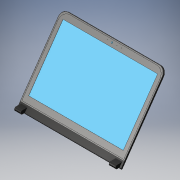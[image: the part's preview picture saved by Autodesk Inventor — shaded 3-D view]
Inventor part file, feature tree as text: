
AUTODESK INVENTOR PART (.ipt)
format: ipt  version: 2025 (Build 290162000, 162)  size: 221,184 bytes
history: native  units: in
note: dims shown in document units (in); Inventor stores cm internally (conversion verified against a paired STEP export)
features: sketch x10, extrude x7, hole x2, move_body x2, other x1, plane x1, pattern_linear x1
ambient origin geometry x8: Origin, YZ Plane, XZ Plane, XY Plane, X Axis, Y Axis, Z Axis, Center Point
bodies: Solid1 (feature_tree)
feature tree (24):
  other  "MONITOR"
  extrude  "SCREEN"  Depth=12.9921in
  extrude  "CAMERA"  Depth=0.1969in TaperAngle=0.0deg
  hole  "CAMERA "  [1 undecoded]
  hole  "AESTHETICS"  [1 undecoded]
  extrude  "SIDE BAND"  Depth=9.0354in
  extrude  "SIDE BAND 1"  Depth=12.9528in
  extrude  "CUT"  Depth=12.7165in
  extrude  "ROUND BASE"  Depth=0.9252in
  plane  "Work Plane1"
  extrude  "HINGE"  Depth=12.9921in TaperAngle=0.0deg
  pattern_linear  "HINGE 1"  Count1=33 Spacing1=0.0in
  move_body  "Move Body1"
  move_body  "Move Body2"
  sketch  "Sketch1"  dims[d2=12.9921in d3=9.8425in]
  sketch  "Sketch2"  dims[d4=0.7874in d5=0.1969in d6=0.0in]
  sketch  "Sketch3"  dims[d9=11.811in d10=7.4803in]
  sketch  "Sketch4"  dims[d11=0.0197in d12=0.0in d14=0.0098in d15=0.0in]
  sketch  "Sketch5"  dims[d16=0.0394in d17=0.2953in d18=0.1476in d19=0.0984in d20=90.0deg d21=0.0039in d22=0.8108in]
  sketch  "Sketch6"  dims[d23=0.0394in d24=0.2953in d25=0.1476in d26=0.0984in d27=90.0deg d28=0.0039in d29=0.8108in d36=9.0354in]
  sketch  "Sketch7"  dims[d37=0.8071in d38=12.9528in]
  sketch  "Sketch8"  dims[d39=0.0059in d40=0.0in d47=12.7165in]
  sketch  "Sketch9"  dims[d48=8.7992in d49=0.9252in]
  sketch  "Sketch10"  dims[d50=0.0059in d51=0.0in d52=12.9921in d53=0.0in d54=12.9921in d55=0.0in d56=5.9055in d58=0.315in d60=0.5512in d62=0.6311in d63=0.2258in d64=0.7874in d65=0.0in d66=0.7874in d68=11.811in d69=-0.2405in d70=0.3937in d71=0.0in d72=0.0in]
note: 2 required parameter values undecoded (feature->parameter linkage not recoverable at this tier; creation-order binding heuristic only, values carry confidence <= 0.55)
